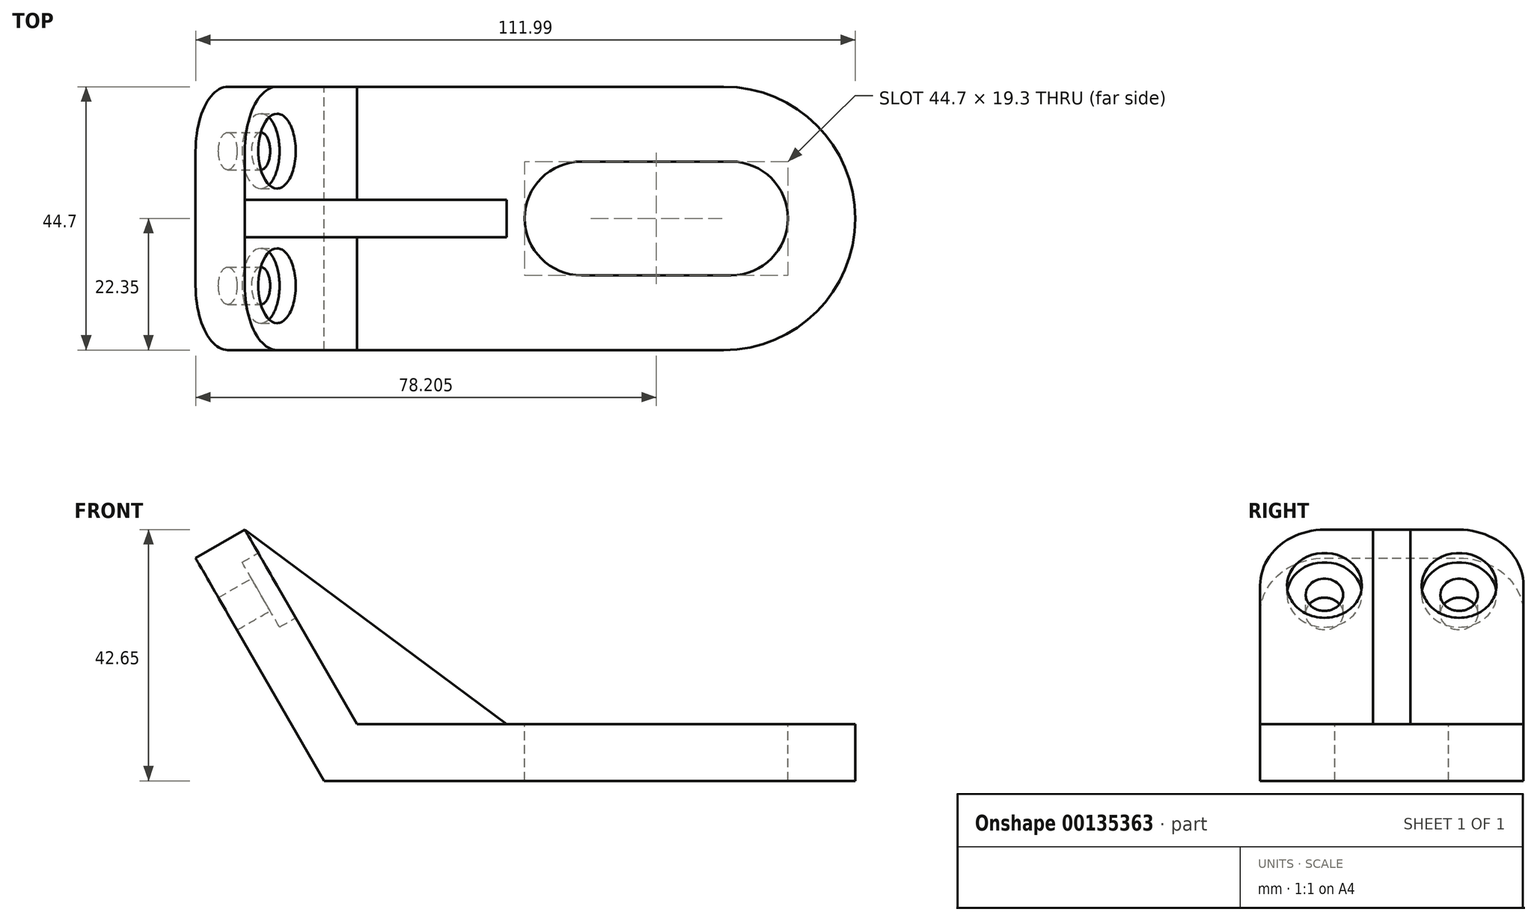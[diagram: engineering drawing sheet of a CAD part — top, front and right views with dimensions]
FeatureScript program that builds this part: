
annotation { "Feature Type Name" : "Feature", "Feature Type Description" : "" }
export const myFeature = defineFeature(function(context is Context, id is Id, definition is map)
    precondition{}
    {
        {
            var Q0;
            Q0=qCreatedBy(makeId("Front.planeOp"),FACE);
            var sketch = newSketch(context, id + "F0", { "sketchPlane" : qUnion([Q0])});
            skLineSegment(sketch, "E0", {"start": v(-33.64, 42.65) * mm, "end": v(-14.6, 9.65) * mm});
            skLineSegment(sketch, "E1", {"start": v(-14.6, 9.65) * mm, "end": v(69.99, 9.65) * mm});
            skLineSegment(sketch, "E2", {"start": v(69.99, 9.65) * mm, "end": v(69.99, 0) * mm});
            skLineSegment(sketch, "E3", {"start": v(69.99, 0) * mm, "end": v(-20.17, 0) * mm});
            skLineSegment(sketch, "E4", {"start": v(-20.17, 0) * mm, "end": v(-42, 37.82) * mm});
            skLineSegment(sketch, "E5", {"start": v(-42, 37.82) * mm, "end": v(-33.64, 42.65) * mm});
            skLineSegment(sketch, "E6", {"start": v(-33.64, 42.65) * mm, "end": v(10.8, 9.65) * mm});
            skSolve(sketch);
        }
        {
            var Q0;
            {var subQ3=sQuery(id+"F0.wireOp",EDGE,"E0");Q0=makeQuery(id+"F0.imprint","IMPRINT",FACE,{"disambiguationData":[TD([[makeQuery(id+"F0.imprint","IMPRINT",EDGE,{"derivedFrom":subQ3}),-1.0]])]});}
            extrude(context, id + "F1", {"entities" : qUnion([Q0]), "endBound" : BoundingType.SYMMETRIC, "depth" : 44.7 * mm});
        }
        {
            var Q0;
            {var subQ0=sQuery(id+"F0.wireOp",EDGE,"E0");Q0=makeQuery(id+"F0.imprint","IMPRINT",FACE,{"disambiguationData":[TD([[makeQuery(id+"F0.imprint","IMPRINT",EDGE,{"derivedFrom":subQ0}),1.0]])]});}
            extrude(context, id + "F2", {"entities" : qUnion([Q0]), "operationType" : NewBodyOperationType.ADD, "endBound" : BoundingType.SYMMETRIC, "depth" : 6.35 * mm});
        }
        {
            var Q0;
            Q0=makeQuery(id+"F1.opExtrude","SWEPT_FACE",FACE,{"disambiguationData":[OSD([sQuery(id+"F0.wireOp",EDGE,"E1")])]});
            var sketch = newSketch(context, id + "F3", { "sketchPlane" : qUnion([Q0])});
            skLineSegment(sketch, "E7", {"start": v(-14.6, 0) * mm, "end": v(23.5, 0) * mm});
            skPoint(sketch, "E7.startSnap0", {"position": v(-14.6, 12.76) * mm});
            skPoint(sketch, "E7.endSnap0", {"position": v(10.8, 0) * mm});
            skLineSegment(sketch, "E8", {"start": v(23.5, 0) * mm, "end": v(48.9, 0) * mm});
            skArc(sketch, "E9", {"start": v(23.5, 9.65) * mm, "mid": v(13.85, 0) * mm, "end": v(23.5, -9.65) * mm});
            skArc(sketch, "E10", {"start": v(48.9, -9.65) * mm, "mid": v(58.56, 0) * mm, "end": v(48.9, 9.65) * mm});
            skLineSegment(sketch, "E11", {"start": v(23.5, 9.65) * mm, "end": v(48.9, 9.65) * mm});
            skLineSegment(sketch, "E12", {"start": v(23.5, -9.65) * mm, "end": v(48.9, -9.65) * mm});
            skLineSegment(sketch, "E13", {"start": v(48.81, 22.35) * mm, "end": v(48.9, -22.35) * mm, "construction": true});
            skCircle(sketch, "E14", {"center": v(48.9, 0) * mm, "radius": 22.35 * mm});
            skSolve(sketch);
        }
        {
            var Q0;
            {var subQ3=sQuery(id+"F3.wireOp",EDGE,"E7");var subQ7=sQuery(id+"F3.wireOp",EDGE,"E8");var subQ8=makeQuery(id+"F3.imprint","INTERSECT",VERTEX,{"derivedFrom":[subQ3,subQ7]});Q0=makeQuery(id+"F3.imprint","IMPRINT",FACE,{"disambiguationData":[TD([[makeQuery(id+"F3.imprint","IMPRINT",EDGE,{"disambiguationData":[TD([[subQ8,1.0]])],"derivedFrom":subQ3}),1.0]])]});}
            var Q1;
            {var subQ3=sQuery(id+"F3.wireOp",EDGE,"E7");var subQ7=sQuery(id+"F3.wireOp",EDGE,"E8");var subQ9=makeQuery(id+"F3.imprint","INTERSECT",VERTEX,{"derivedFrom":[subQ3,subQ7]});Q1=makeQuery(id+"F3.imprint","IMPRINT",FACE,{"disambiguationData":[TD([[makeQuery(id+"F3.imprint","IMPRINT",EDGE,{"disambiguationData":[TD([[subQ9,1.0]])],"derivedFrom":subQ3}),-1.0]])]});}
            var Q2;
            {var subQ4=sQuery(id+"F3.wireOp",EDGE,"E10");Q2=makeQuery(id+"F3.imprint","IMPRINT",FACE,{"disambiguationData":[TD([[makeQuery(id+"F3.imprint","IMPRINT",EDGE,{"derivedFrom":subQ4}),1.0]])]});}
            extrude(context, id + "F4", {"entities" : qUnion([Q0, Q1, Q2]), "operationType" : NewBodyOperationType.REMOVE, "oppositeDirection" : true, "depth" : 1143 * mm});
        }
        {
            var Q0;
            Q0=makeQuery(id+"F1.opExtrude","SWEPT_FACE",FACE,{"disambiguationData":[OSD([sQuery(id+"F0.wireOp",EDGE,"E4")])]});
            var sketch = newSketch(context, id + "F5", { "sketchPlane" : qUnion([Q0])});
            skLineSegment(sketch, "E15", {"start": v(-22.35, 42.83) * mm, "end": v(22.35, 42.83) * mm, "construction": true});
            skLineSegment(sketch, "E16", {"start": v(-11.43, 53.76) * mm, "end": v(-11.43, 10.08) * mm, "construction": true});
            skLineSegment(sketch, "E17", {"start": v(11.43, 53.76) * mm, "end": v(11.43, 10.08) * mm, "construction": true});
            skCircle(sketch, "E18", {"center": v(-11.43, 42.83) * mm, "radius": 3.18 * mm});
            skCircle(sketch, "E19", {"center": v(-11.43, 42.83) * mm, "radius": 6.35 * mm});
            skCircle(sketch, "E20", {"center": v(11.43, 42.83) * mm, "radius": 3.18 * mm});
            skCircle(sketch, "E21", {"center": v(11.43, 42.83) * mm, "radius": 6.35 * mm});
            skSolve(sketch);
        }
        {
            var Q0;
            {var subQ0=sQuery(id+"F0.wireOp",EDGE,"E6");var subQ1=sQuery(id+"F0.wireOp",EDGE,"E1");var subQ2=sQuery(id+"F0.wireOp",EDGE,"E0");Q0=makeQuery(id+"F2.boolean.opBoolean","SPLIT",FACE,{"disambiguationData":[TD([makeQuery(id+"F2.opExtrude","CAP_FACE",FACE,{"disambiguationData":[OSD([subQ2,subQ1,subQ0])],"isStart":true})])],"derivedFrom":makeQuery(id+"F1.opExtrude","SWEPT_FACE",FACE,{"disambiguationData":[OSD([subQ2])]})});}
            var sketch = newSketch(context, id + "F6", { "sketchPlane" : qUnion([Q0])});
            skCircle(sketch, "E22.0", {"center": v(11.43, 42.83) * mm, "radius": 6.35 * mm});
            skCircle(sketch, "E22.1", {"center": v(11.43, 42.83) * mm, "radius": 3.18 * mm});
            skSolve(sketch);
        }
        {
            var Q0;
            Q0 = qSketchRegion(id + "F6", true);
            extrude(context, id + "F7", {"entities" : qUnion([Q0]), "operationType" : NewBodyOperationType.REMOVE, "oppositeDirection" : true, "depth" : 3.17 * mm});
        }
        {
            var Q0;
            {var subQ0=sQuery(id+"F0.wireOp",EDGE,"E6");var subQ1=sQuery(id+"F0.wireOp",EDGE,"E1");var subQ2=sQuery(id+"F0.wireOp",EDGE,"E0");Q0=makeQuery(id+"F2.boolean.opBoolean","SPLIT",FACE,{"disambiguationData":[TD([makeQuery(id+"F2.opExtrude","CAP_FACE",FACE,{"disambiguationData":[OSD([subQ2,subQ1,subQ0])],"isStart":false})])],"derivedFrom":makeQuery(id+"F1.opExtrude","SWEPT_FACE",FACE,{"disambiguationData":[OSD([subQ2])]})});}
            var sketch = newSketch(context, id + "F8", { "sketchPlane" : qUnion([Q0])});
            skCircle(sketch, "E23.0", {"center": v(-11.43, 42.83) * mm, "radius": 6.35 * mm});
            skCircle(sketch, "E23.1", {"center": v(-11.43, 42.83) * mm, "radius": 3.18 * mm});
            skSolve(sketch);
        }
        {
            var Q0;
            Q0 = qSketchRegion(id + "F8", true);
            extrude(context, id + "F9", {"entities" : qUnion([Q0]), "operationType" : NewBodyOperationType.REMOVE, "oppositeDirection" : true, "depth" : 3.17 * mm});
        }
        {
            var Q0;
            {var subQ0=sQuery(id+"F0.wireOp",EDGE,"E6");var subQ1=sQuery(id+"F0.wireOp",EDGE,"E1");var subQ2=sQuery(id+"F0.wireOp",EDGE,"E0");Q0=makeQuery(id+"F9.boolean.opBoolean","SPLIT",FACE,{"disambiguationData":[TD([makeQuery(id+"F9.opExtrude","SWEPT_FACE",FACE,{"disambiguationData":[OSD([sQuery(id+"F8.wireOp",EDGE,"E23.1")])]})])],"derivedFrom":makeQuery(id+"F2.boolean.opBoolean","SPLIT",FACE,{"disambiguationData":[TD([makeQuery(id+"F2.opExtrude","CAP_FACE",FACE,{"disambiguationData":[OSD([subQ2,subQ1,subQ0])],"isStart":false})])],"derivedFrom":makeQuery(id+"F1.opExtrude","SWEPT_FACE",FACE,{"disambiguationData":[OSD([subQ2])]})})});}
            var Q1;
            {var subQ0=sQuery(id+"F0.wireOp",EDGE,"E6");var subQ1=sQuery(id+"F0.wireOp",EDGE,"E1");var subQ2=sQuery(id+"F0.wireOp",EDGE,"E0");Q1=makeQuery(id+"F7.boolean.opBoolean","SPLIT",FACE,{"disambiguationData":[TD([makeQuery(id+"F7.opExtrude","SWEPT_FACE",FACE,{"disambiguationData":[OSD([sQuery(id+"F6.wireOp",EDGE,"E22.1")])]})])],"derivedFrom":makeQuery(id+"F2.boolean.opBoolean","SPLIT",FACE,{"disambiguationData":[TD([makeQuery(id+"F2.opExtrude","CAP_FACE",FACE,{"disambiguationData":[OSD([subQ2,subQ1,subQ0])],"isStart":true})])],"derivedFrom":makeQuery(id+"F1.opExtrude","SWEPT_FACE",FACE,{"disambiguationData":[OSD([subQ2])]})})});}
            extrude(context, id + "F10", {"entities" : qUnion([Q0, Q1]), "operationType" : NewBodyOperationType.REMOVE, "endBound" : BoundingType.THROUGH_ALL, "oppositeDirection" : true, "depth" : 25.4 * mm});
        }
        {
            var Q0;
            Q0=makeQuery(id+"F1.opExtrude","CAP_EDGE",EDGE,{"disambiguationData":[OSD([sQuery(id+"F0.wireOp",EDGE,"E5")])],"isStart":false});
            var Q1;
            Q1=makeQuery(id+"F1.opExtrude","CAP_EDGE",EDGE,{"disambiguationData":[OSD([sQuery(id+"F0.wireOp",EDGE,"E5")])],"isStart":true});
            fillet(context, id + "F11", {"entities" : qUnion([Q0, Q1]), "radius" : 10.92 * mm, "tangentPropagation" : true, "allowEdgeOverflow" : false});
        }
        {
            var Q0;
            Q0=makeQuery(id+"F1.opExtrude","CAP_EDGE",EDGE,{"disambiguationData":[OSD([sQuery(id+"F0.wireOp",EDGE,"E2")])],"isStart":true});
            var Q1;
            Q1=makeQuery(id+"F1.opExtrude","CAP_EDGE",EDGE,{"disambiguationData":[OSD([sQuery(id+"F0.wireOp",EDGE,"E2")])],"isStart":false});
            fillet(context, id + "F12", {"entities" : qUnion([Q0, Q1]), "radius" : 22.35 * mm, "tangentPropagation" : true, "allowEdgeOverflow" : false});
        }
    });
